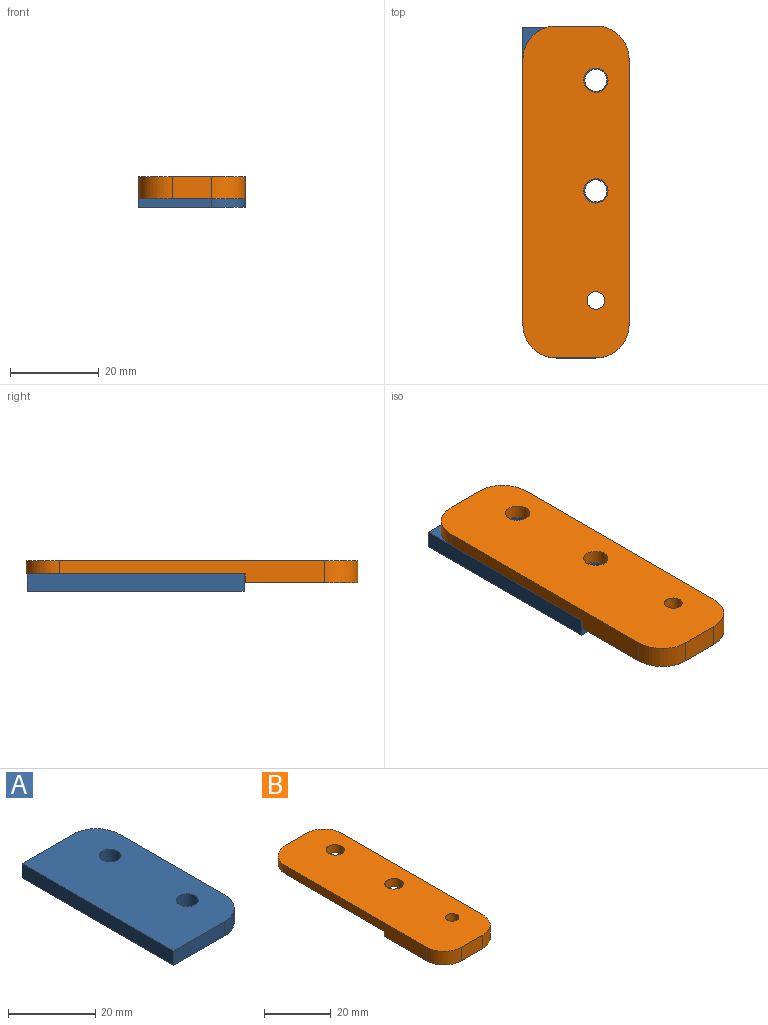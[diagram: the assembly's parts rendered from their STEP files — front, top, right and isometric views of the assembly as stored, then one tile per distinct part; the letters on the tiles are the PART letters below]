
ASSEMBLY  parts=2 mates=1
PART A: 10 faces, bbox 24x49x4 mm
  f0: plane 34x4mm, normal (1,0,0), area 136mm2, adj f4,f5,f6,f7
  f1: plane 16.5x4mm, normal (0,1,0), area 66mm2, adj f2,f4,f5,f6
  f2: plane 49x4mm, normal (-1,0,0), area 196mm2, adj f1,f3,f4,f5
  f3: plane 16.5x4mm, normal (0,-1,0), area 66mm2, adj f2,f4,f5,f7
  f4: plane 49x24mm, normal (0,0,1), area 1112.6mm2, adj f0,f1,f2,f3,f6,f7,f8,f9
  f5: plane 49x24mm, normal (0,0,-1), area 1112.6mm2, adj f0,f1,f2,f3,f6,f7,f8,f9
  f6: cylinder r=7.5mm len=7.5mm, axis (0,0,1), area 47.1mm2, adj f0,f1,f4,f5
  f7: cylinder r=7.5mm len=7.5mm, axis (0,0,-1), area 47.1mm2, adj f0,f3,f4,f5
  f8: cylinder r=2.5mm len=5mm, axis (0,0,1), area 62.8mm2, adj f4,f5
  f9: cylinder r=2.5mm len=5mm, axis (0,0,1), area 62.8mm2, adj f4,f5
PART B: 16 faces, bbox 24x75x5 mm
  f0: plane 60x5mm, normal (-1,0,0), area 216mm2, adj f6,f7,f11,f12,f13,f15
  f1: cylinder r=2.75mm len=5.5mm, axis (0,0,1), area 51.8mm2, adj f6,f15
  f2: cylinder r=2.75mm len=5.5mm, axis (0,0,1), area 51.8mm2, adj f6,f15
  f3: plane 9x5mm, normal (0,-1,0), area 45mm2, adj f6,f7,f9,f12
  f4: plane 60x5mm, normal (1,0,0), area 231mm2, adj f6,f7,f9,f10,f14,f15
  f5: plane 9x3mm, normal (0,1,0), area 27mm2, adj f6,f10,f11,f15
  f6: plane 75x24mm, normal (0,0,1), area 1691.6mm2, adj f0,f1,f2,f3,f4,f5,f8,f9
  f7: plane 33x24mm, normal (0,0,-1), area 587.4mm2, adj f0,f3,f4,f8,f9,f12,f13,f14
  f8: cylinder r=2mm len=5mm, axis (0,0,1), area 62.8mm2, adj f6,f7
  f9: cylinder r=7.5mm len=7.5mm, axis (0,0,1), area 58.9mm2, adj f3,f4,f6,f7
  f10: cylinder r=7.5mm len=7.5mm, axis (0,0,-1), area 35.3mm2, adj f4,f5,f6,f15
  f11: cylinder r=7.5mm len=7.5mm, axis (0,0,1), area 35.3mm2, adj f0,f5,f6,f15
  f12: cylinder r=7.5mm len=7.5mm, axis (0,0,-1), area 58.9mm2, adj f0,f3,f6,f7
  f13: plane 16.5x2mm, normal (0,1,0), area 33mm2, adj f0,f7,f14,f15
  f14: cylinder r=7.5mm len=7.5mm, axis (0,0,-1), area 23.6mm2, adj f4,f7,f13,f15
  f15: plane 49.5x24mm, normal (0,0,-1), area 1104.3mm2, adj f0,f1,f2,f4,f5,f10,f11,f13
PLACE A t=(-68.04,-17.88,8.32)mm
PLACE B t=(-68.04,-30.63,10.32)mm
MATE fastened A.f9 <-> B.f2  axis (0,0,1) through (-63.54,-5.38,12.32)mm
